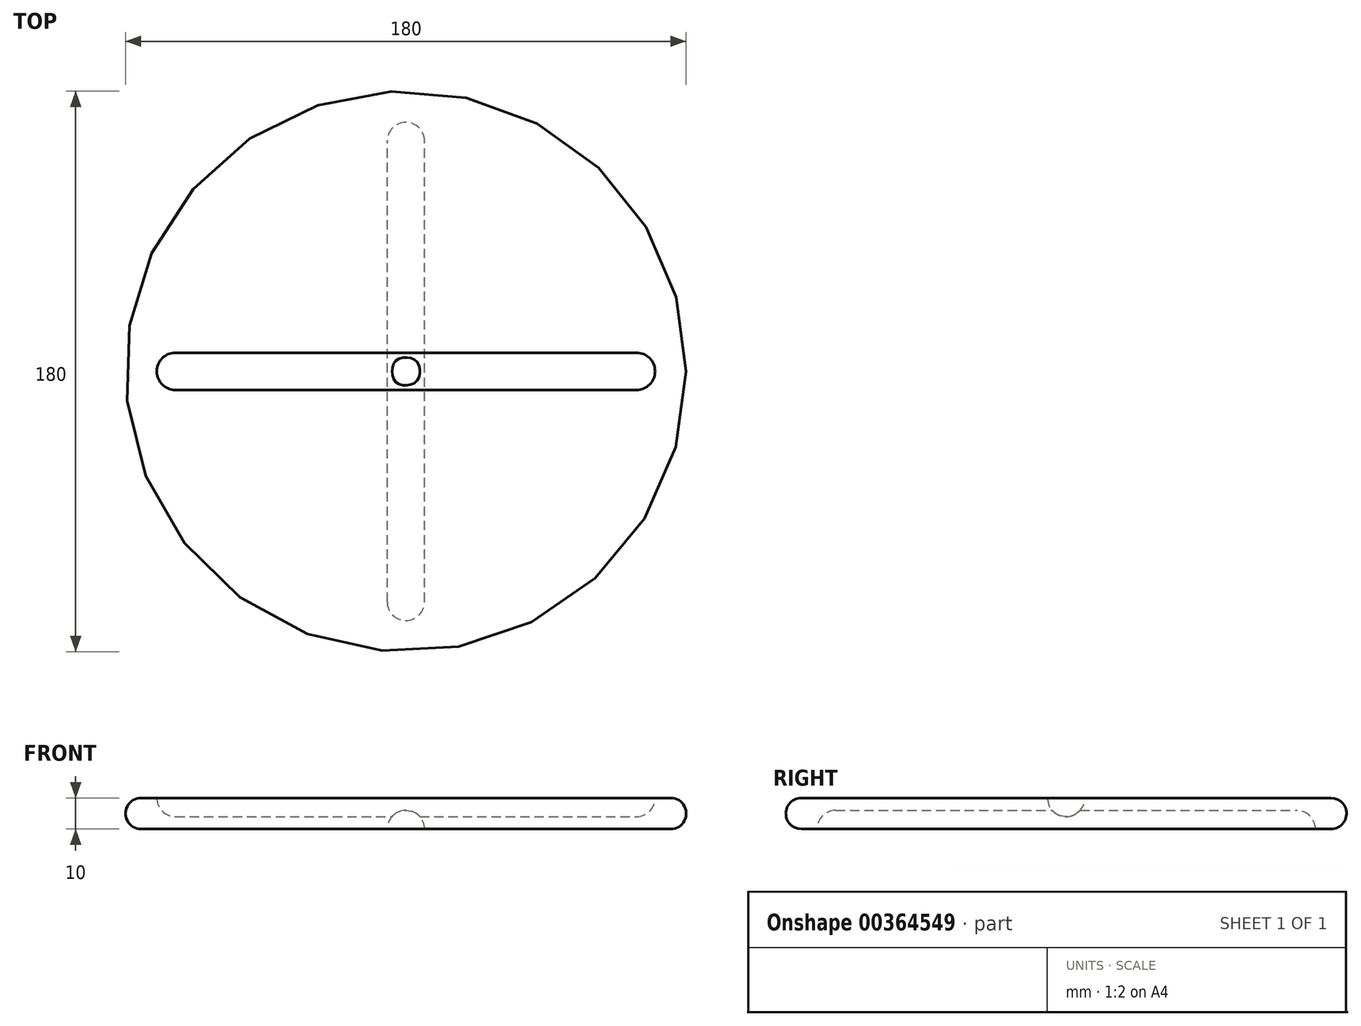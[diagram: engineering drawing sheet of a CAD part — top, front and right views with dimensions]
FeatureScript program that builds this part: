
annotation { "Feature Type Name" : "Feature", "Feature Type Description" : "" }
export const myFeature = defineFeature(function(context is Context, id is Id, definition is map)
    precondition{}
    {
        {
            var Q0;
            Q0=qCreatedBy(makeId("Top.planeOp"),FACE);
            var sketch = newSketch(context, id + "F0", { "sketchPlane" : qUnion([Q0])});
            skCircle(sketch, "E0", {"center": v(0, 0) * mm, "radius": 90 * mm});
            skSolve(sketch);
        }
        {
            var Q0;
            Q0=makeQuery(id+"F0.imprint","IMPRINT",FACE,{"disambiguationData":[TD([[makeQuery(id+"F0.imprint","IMPRINT",EDGE,{"derivedFrom":sQuery(id+"F0.wireOp",EDGE,"E0")}),1.0]])]});
            extrude(context, id + "F1", {"entities" : qUnion([Q0]), "depth" : 10 * mm});
        }
        {
            var Q0;
            Q0=makeQuery(id+"F1.opExtrude","CAP_EDGE",EDGE,{"disambiguationData":[OSD([sQuery(id+"F0.wireOp",EDGE,"E0")])],"isStart":false});
            var Q1;
            Q1=makeQuery(id+"F1.opExtrude","CAP_EDGE",EDGE,{"disambiguationData":[OSD([sQuery(id+"F0.wireOp",EDGE,"E0")])],"isStart":true});
            fillet(context, id + "F2", {"entities" : qUnion([Q0, Q1]), "radius" : 5 * mm, "tangentPropagation" : true, "allowEdgeOverflow" : false});
        }
        {
            var Q0;
            Q0=qCreatedBy(makeId("Front.planeOp"),FACE);
            var sketch = newSketch(context, id + "F3", { "sketchPlane" : qUnion([Q0])});
            skCircle(sketch, "E1", {"center": v(0, 0) * mm, "radius": 6 * mm});
            skSolve(sketch);
        }
        {
            var Q0;
            Q0=makeQuery(id+"F3.imprint","IMPRINT",FACE,{"disambiguationData":[TD([[makeQuery(id+"F3.imprint","IMPRINT",EDGE,{"derivedFrom":sQuery(id+"F3.wireOp",EDGE,"E1")}),1.0]])]});
            extrude(context, id + "F4", {"entities" : qUnion([Q0]), "operationType" : NewBodyOperationType.REMOVE, "depth" : 80 * mm, "hasSecondDirection" : true, "secondDirectionOppositeDirection" : true, "secondDirectionDepth" : 80 * mm});
        }
        {
            var Q0;
            Q0=qCreatedBy(makeId("Right.planeOp"),FACE);
            var sketch = newSketch(context, id + "F5", { "sketchPlane" : qUnion([Q0])});
            skCircle(sketch, "E2", {"center": v(0, 10) * mm, "radius": 6 * mm});
            skSolve(sketch);
        }
        {
            var Q0;
            Q0=makeQuery(id+"F5.imprint","IMPRINT",FACE,{"disambiguationData":[TD([[makeQuery(id+"F5.imprint","IMPRINT",EDGE,{"derivedFrom":sQuery(id+"F5.wireOp",EDGE,"E2")}),1.0]])]});
            extrude(context, id + "F6", {"entities" : qUnion([Q0]), "operationType" : NewBodyOperationType.REMOVE, "oppositeDirection" : true, "depth" : 80 * mm, "hasSecondDirection" : true, "secondDirectionOppositeDirection" : false, "secondDirectionDepth" : 80 * mm});
        }
        {
            var Q0;
            Q0=makeQuery(id+"F6.boolean.opBoolean","COPY",EDGE,{"derivedFrom":makeQuery(id+"F6.opExtrude","CAP_EDGE",EDGE,{"disambiguationData":[OSD([sQuery(id+"F5.wireOp",EDGE,"E2")])],"isStart":true})});
            var Q1;
            Q1=makeQuery(id+"F6.boolean.opBoolean","COPY",EDGE,{"derivedFrom":makeQuery(id+"F6.opExtrude","CAP_EDGE",EDGE,{"disambiguationData":[OSD([sQuery(id+"F5.wireOp",EDGE,"E2")])],"isStart":false})});
            fillet(context, id + "F7", {"entities" : qUnion([Q0, Q1]), "radius" : 6 * mm, "tangentPropagation" : true, "allowEdgeOverflow" : false});
        }
        {
            var Q0;
            Q0=makeQuery(id+"F4.boolean.opBoolean","COPY",EDGE,{"derivedFrom":makeQuery(id+"F4.opExtrude","CAP_EDGE",EDGE,{"disambiguationData":[OSD([sQuery(id+"F3.wireOp",EDGE,"E1")])],"isStart":false})});
            var Q1;
            Q1=makeQuery(id+"F4.boolean.opBoolean","COPY",EDGE,{"derivedFrom":makeQuery(id+"F4.opExtrude","CAP_EDGE",EDGE,{"disambiguationData":[OSD([sQuery(id+"F3.wireOp",EDGE,"E1")])],"isStart":true})});
            fillet(context, id + "F8", {"entities" : qUnion([Q0, Q1]), "radius" : 6 * mm, "tangentPropagation" : true, "allowEdgeOverflow" : false});
        }
    });
